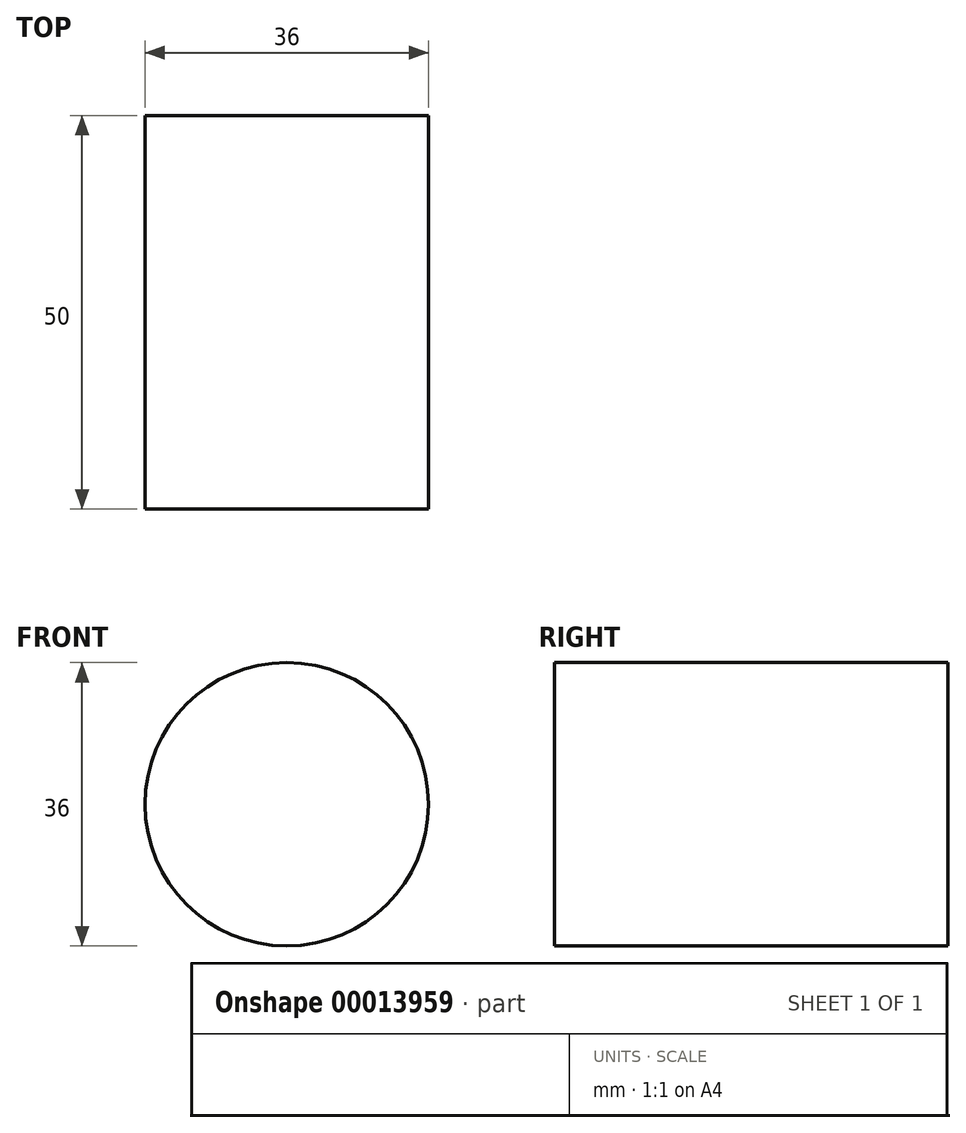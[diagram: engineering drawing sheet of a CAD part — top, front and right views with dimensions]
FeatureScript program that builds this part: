
annotation { "Feature Type Name" : "Feature", "Feature Type Description" : "" }
export const myFeature = defineFeature(function(context is Context, id is Id, definition is map)
    precondition{}
    {
        {
            var Q0;
            Q0=qCreatedBy(makeId("Front.planeOp"),FACE);
            var sketch = newSketch(context, id + "F0", { "sketchPlane" : qUnion([Q0])});
            skCircle(sketch, "E0", {"center": v(0, 0) * mm, "radius": 18 * mm});
            skSolve(sketch);
        }
        {
            var Q0;
            Q0=makeQuery(id+"F0.imprint","IMPRINT",FACE,{"disambiguationData":[TD([[makeQuery(id+"F0.imprint","IMPRINT",EDGE,{"derivedFrom":sQuery(id+"F0.wireOp",EDGE,"E0")}),1.0]])]});
            extrude(context, id + "F1", {"entities" : qUnion([Q0]), "depth" : 50 * mm});
        }
    });
